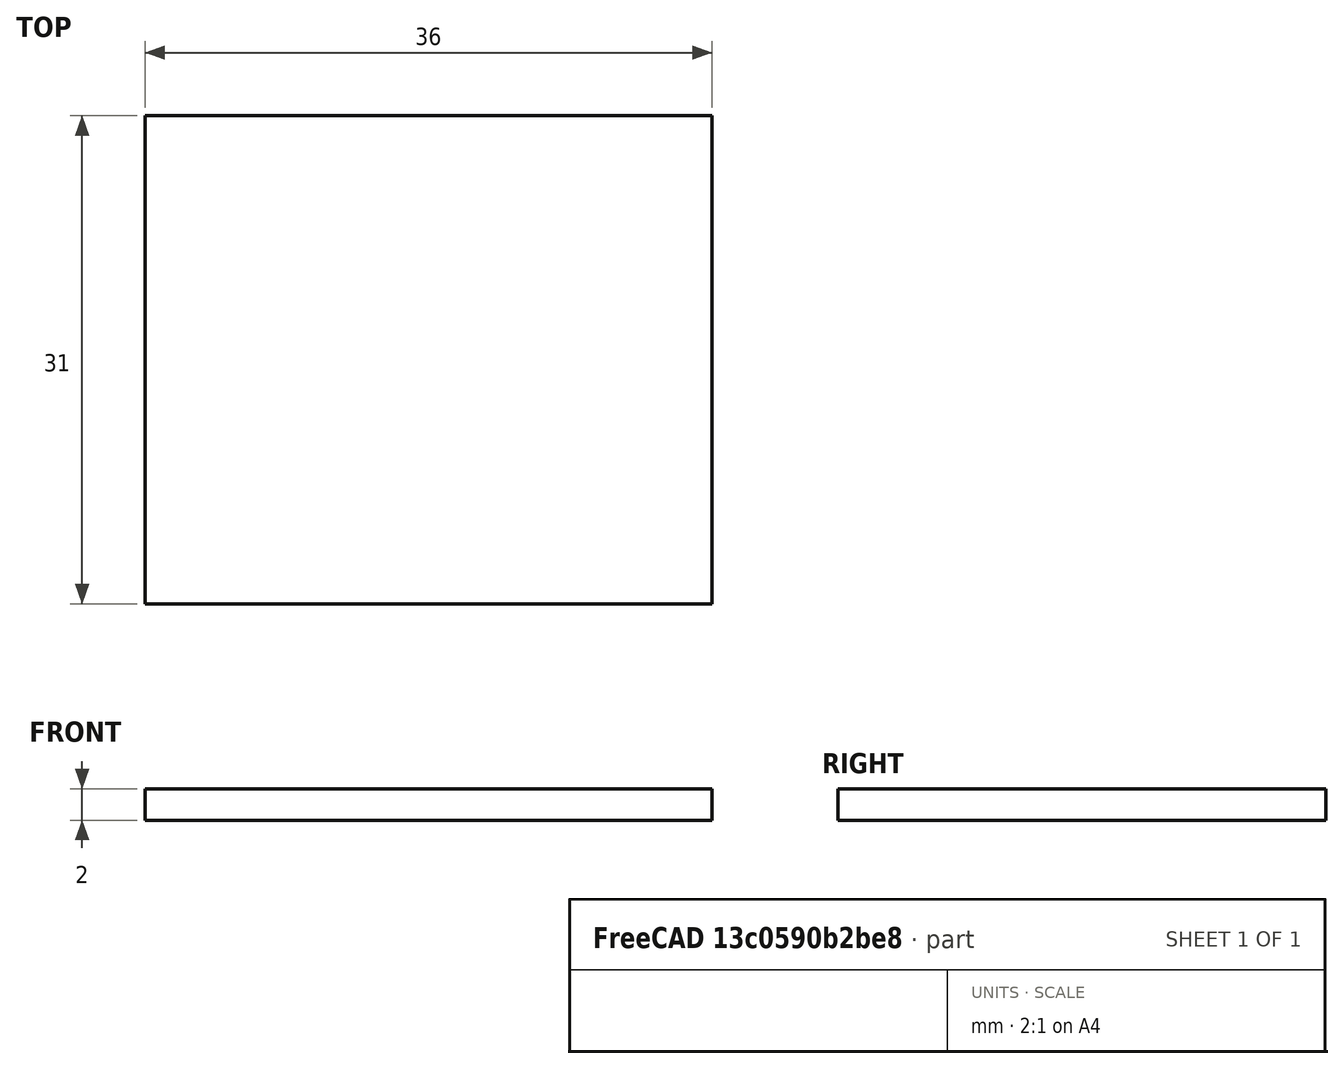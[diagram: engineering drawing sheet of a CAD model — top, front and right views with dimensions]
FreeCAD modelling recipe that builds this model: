
FCSTD DOCUMENT  (FreeCAD 1.0R39319 (Git))
Label: motor_encoder
License: All rights reserved
LicenseURL: http://en.wikipedia.org/wiki/All_rights_reserved
objects: Sketcher::SketchObject×1, PartDesign::Pad×1, PartDesign::Body×1
note: 6 computed .brp shape members not serialized (recipe doc carries the construction recipe); baked Part::Feature solids carry a one-line shape summary decoded from their .brp

FEATURE [Sketcher::SketchObject] Sketch
  ArcFitTolerance = 1e-06
  AttachmentSupport = -> [XY_Plane]
  FullyConstrained = true
  MakeInternals = false
  MapMode = 5
  sketch-geometry (4):
    g0: LineSegment StartX=2 StartY=35 StartZ=0 EndX=2 EndY=4 EndZ=0
    g1: LineSegment StartX=2 StartY=4 StartZ=0 EndX=38 EndY=4 EndZ=0
    g2: LineSegment StartX=38 StartY=4 StartZ=0 EndX=38 EndY=35 EndZ=0
    g3: LineSegment StartX=38 StartY=35 StartZ=0 EndX=2 EndY=35 EndZ=0
  constraints (12):
    c: Coincident(g0,g1)
    c: Coincident(g1,g2)
    c: Coincident(g2,g3)
    c: Coincident(g3,g0)
    c: Vertical(g0)
    c: Vertical(g2)
    c: Horizontal(g1)
    c: Horizontal(g3)
    c: DistanceY(g0,g0) = 31
    c: DistanceX(g0,g2) = 36
    c: DistanceY(g-1,g0) = 4
    c: DistanceX(g-1,g0) = 2
FEATURE [PartDesign::Pad] Pad
  Direction = (0,0,1)
  Length = 2
  Length2 = 10
  Profile = -> Sketch
  ReferenceAxis = -> Sketch [N_Axis]
  Suppressed = false
  Type = 0
FEATURE [PartDesign::Body] Body
  AllowCompound = false
  Group = -> [Sketch,Pad]
  Origin = -> Origin
  Tip = -> Pad
